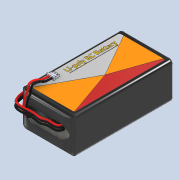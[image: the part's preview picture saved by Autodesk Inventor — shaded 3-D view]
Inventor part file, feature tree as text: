
AUTODESK INVENTOR PART (.ipt)
format: ipt  version: 2020 (Build 240168000, 168)  size: 1,844,736 bytes
history: native  units: mm
features: sketch x29, extrude x17, fillet x5, sweep x5, emboss x2, plane x2, projected_geometry x1
ambient origin geometry x8: Origin, YZ Plane, XZ Plane, XY Plane, X Axis, Y Axis, Z Axis, Center Point
bodies: Solid1 (feature_tree), Solid2 (feature_tree), Solid3 (feature_tree), Solid4 (feature_tree), Solid5 (feature_tree), Solid6 (feature_tree), Solid7 (feature_tree), Solid9 (feature_tree), Solid10 (feature_tree), Solid11 (feature_tree), Solid12 (feature_tree), Solid13 (feature_tree), Solid14 (feature_tree), Solid15 (feature_tree), Solid16 (feature_tree), Solid17 (feature_tree)
feature tree (61):
  extrude  "Extrusion1"  Depth=55.0mm
  fillet  "Fillet1"  Radius=20.0mm
  fillet  "Fillet2"  Radius=2.0mm
  fillet  "Fillet3"  Radius=2.0mm
  extrude  "Extrusion2"  Depth=5.0mm
  fillet  "Fillet4"  Radius=0.25mm
  extrude  "Extrusion3"  Depth=3.0mm TaperAngle=45.0deg
  fillet  "Fillet5"  Radius=0.1mm
  extrude  "Extrusion4"  Depth=0.01mm TaperAngle=0.0deg
  extrude  "Extrusion5"  Depth=0.01mm TaperAngle=0.0deg
  extrude  "Extrusion6"  Depth=0.01mm TaperAngle=0.0deg
  extrude  "Extrusion7"  Depth=0.01mm TaperAngle=0.0deg
  extrude  "Extrusion8"  Depth=0.01mm TaperAngle=0.0deg
  extrude  "Extrusion9"  Depth=0.01mm TaperAngle=0.0deg
  emboss  "Emboss1"
  extrude  "Extrusion10"  Depth=0.2mm
  emboss  "Emboss2"
  extrude  "Extrusion11"  Depth=0.005mm TaperAngle=0.0deg
  plane  "Work Plane2"
  sketch  "Sketch14"  dims[d47=1.0mm d48=1.0mm]
  sweep  "Sweep2"
  sweep  "Sweep3"
  sweep  "Sweep4"
  sweep  "Sweep5"
  sweep  "Sweep6"
  extrude  "Extrusion12"  TaperAngle=0.0deg  [1 undecoded]
  extrude  "Extrusion13"  TaperAngle=0.0deg  [1 undecoded]
  extrude  "Extrusion14"  Depth=0.2mm TaperAngle=0.0deg
  plane  "Work Plane3"
  extrude  "Extrusion15"  Depth=0.633711mm
  extrude  "Extrusion16"  Depth=0.3mm
  sketch  "Sketch1"  dims[d0=29.0mm d1=55.0mm d2=20.0mm d3=0.0mm d4=2.0mm d5=2.0mm]
  sketch  "Sketch2"  dims[d6=1.0mm d8=5.0mm d9=0.25mm d10=30.0deg]
  sketch  "Sketch3"  dims[d11=6.25mm d12=3.0mm d13=45.0deg d14=0.1mm]
  sketch  "Sketch4"  dims[d15=1.0mm d16=0.01mm d17=0.0mm]
  sketch  "Sketch8"  dims[d27=1.0mm d28=0.01mm d29=0.0mm]
  sketch  "Sketch10"  dims[d33=0.005mm d34=0.0mm d35=0.2mm]
  sketch  "Sketch11"  dims[d36=0.005mm d37=0.0mm d38=0.005mm d39=0.0mm]
  sketch  "Sketch12"  dims[d41=0.005mm d42=0.0mm d44=26.25mm]
  sketch  "Sketch13"  dims[d45=1.0mm d46=1.0mm]
  sketch  "Sketch16"  dims[d49=1.0mm]
  sketch  "Sketch18"  dims[d59=1.0mm d60=1.0mm d61=1.0mm d62=1.0mm d63=1.0mm d64=0.0mm d65=0.0mm]
  sketch  "Sketch20"  dims[d73=1.0mm d74=1.0mm d75=1.0mm d76=1.0mm d77=1.0mm d78=0.0mm d79=0.0mm]
  sketch  "Sketch21"  dims[d80=0.0mm d81=0.0mm d82=0.2mm d83=0.5mm d84=0.0mm d85=0.0mm]
  sketch  "Sketch22"  dims[d86=2.7mm d87=0.0mm d88=0.633711mm]
  sketch  "Sketch25"  dims[d93=0.8mm]
  sketch  "Sketch26"  dims[d94=0.428978mm]
  projected_geometry  "Projected Loop1"
  sketch  "Sketch27"  dims[d95=0.429mm]
  sketch  "Sketch28"  dims[d96=1.0mm d97=0.0mm]
  sketch  "Sketch29"  dims[d98=14.75mm]
  sketch  "Sketch5"  dims[d18=1.0mm d19=0.01mm d20=0.0mm]
  sketch  "Sketch6"  dims[d21=1.0mm d22=0.01mm d23=0.0mm]
  sketch  "Sketch7"  dims[d24=1.0mm d25=0.01mm d26=0.0mm]
  sketch  "Sketch9"  dims[d30=1.0mm d31=0.01mm d32=0.0mm]
  sketch  "Sketch17"  dims[d52=1.0mm d53=1.0mm d54=1.0mm d55=1.0mm d56=1.0mm d57=0.0mm d58=0.0mm]
  sketch  "Sketch19"  dims[d66=1.0mm d67=1.0mm d68=1.0mm d69=1.0mm d70=1.0mm d71=0.0mm d72=0.0mm]
  sketch  "Sketch23"  dims[d89=0.633711mm d90=0.3mm]
  sketch  "Sketch24"  dims[d91=0.8mm d92=0.617mm]
  sketch  "Sketch30"  dims[d99=0.5mm d100=0.5mm d101=0.0mm d102=0.0mm d103=2.25mm d104=0.0mm d105=0.8mm d106=0.8mm d107=0.617mm d108=0.3mm d109=0.429mm d110=0.633711mm d111=0.633711mm d112=0.428978mm d114=0.0mm d115=1.0mm]
  extrude  "Extrusion17"  Depth=0.617mm
note: 2 required parameter values undecoded (feature->parameter linkage not recoverable at this tier; creation-order binding heuristic only, values carry confidence <= 0.55)
